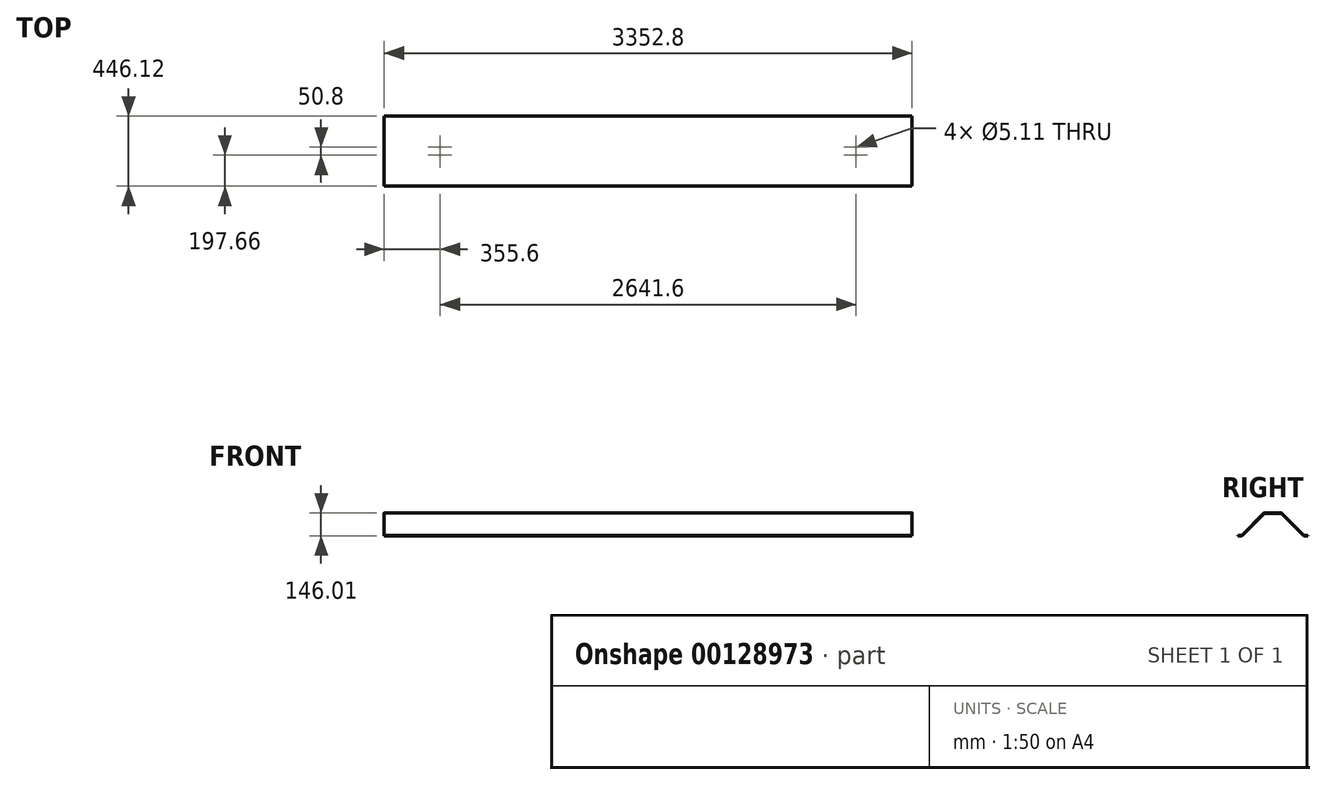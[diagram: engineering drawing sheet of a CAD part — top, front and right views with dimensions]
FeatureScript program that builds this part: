
annotation { "Feature Type Name" : "Feature", "Feature Type Description" : "" }
export const myFeature = defineFeature(function(context is Context, id is Id, definition is map)
    precondition{}
    {
        {
            var Q0;
            Q0=qCreatedBy(makeId("Right.planeOp"),FACE);
            var sketch = newSketch(context, id + "F0", { "sketchPlane" : qUnion([Q0])});
            skLineSegment(sketch, "E0", {"start": v(0, 146) * mm, "end": v(54.94, 146) * mm});
            skLineSegment(sketch, "E1", {"start": v(54.94, 146) * mm, "end": v(198.62, 2.32) * mm});
            skLineSegment(sketch, "E2", {"start": v(198.62, 2.32) * mm, "end": v(223.06, 2.32) * mm});
            skLineSegment(sketch, "E3", {"start": v(223.06, 2.32) * mm, "end": v(223.06, 0) * mm});
            skLineSegment(sketch, "E4", {"start": v(223.06, 0) * mm, "end": v(197.66, 0) * mm});
            skLineSegment(sketch, "E5", {"start": v(197.66, 0) * mm, "end": v(53.97, 143.68) * mm});
            skLineSegment(sketch, "E6", {"start": v(53.98, 143.68) * mm, "end": v(0, 143.68) * mm});
            skLineSegment(sketch, "E7", {"start": v(0, 143.68) * mm, "end": v(0, 146) * mm});
            skLineSegment(sketch, "E8", {"start": v(62.94, 134.72) * mm, "end": v(64.58, 136.37) * mm});
            skSolve(sketch);
        }
        {
            var Q0;
            {var subQ1=sQuery(id+"F0.wireOp",EDGE,"E2");Q0=makeQuery(id+"F0.imprint","IMPRINT",FACE,{"disambiguationData":[TD([[makeQuery(id+"F0.imprint","IMPRINT",EDGE,{"derivedFrom":subQ1}),-1.0]])]});}
            var Q1;
            {var subQ2=sQuery(id+"F0.wireOp",EDGE,"E0");Q1=makeQuery(id+"F0.imprint","IMPRINT",FACE,{"disambiguationData":[TD([[makeQuery(id+"F0.imprint","IMPRINT",EDGE,{"derivedFrom":subQ2}),-1.0]])]});}
            extrude(context, id + "F1", {"entities" : qUnion([Q0, Q1]), "endBound" : BoundingType.SYMMETRIC, "depth" : 3352.8 * mm});
        }
        {
            var Q0;
            Q0=makeQuery(id+"F1.opExtrude","SWEPT_BODY",BODY,{"disambiguationData":[OSD([sQuery(id+"F0.wireOp",EDGE,"E0"),sQuery(id+"F0.wireOp",EDGE,"E1"),sQuery(id+"F0.wireOp",EDGE,"E2"),sQuery(id+"F0.wireOp",EDGE,"E3"),sQuery(id+"F0.wireOp",EDGE,"E4"),sQuery(id+"F0.wireOp",EDGE,"E5"),sQuery(id+"F0.wireOp",EDGE,"E6"),sQuery(id+"F0.wireOp",EDGE,"E7")])]});
            var Q1;
            Q1=makeQuery(id+"F1.opExtrude","SWEPT_FACE",FACE,{"disambiguationData":[OSD([sQuery(id+"F0.wireOp",EDGE,"E7")])]});
            mirror(context, id + "F2", {"operationType" : NewBodyOperationType.ADD, "entities" : qUnion([Q0]), "mirrorPlane" : qUnion([Q1])});
        }
        {
            var Q0;
            Q0=makeQuery(id+"F2.opPattern","COPY",EDGE,{"derivedFrom":makeQuery(id+"F1.opExtrude","SWEPT_EDGE",EDGE,{"disambiguationData":[OSD([sQuery(id+"F0.wireOp",EDGE,"E0"),sQuery(id+"F0.wireOp",EDGE,"E1")])]}),"instanceName":"1"});
            var Q1;
            Q1=makeQuery(id+"F2.opPattern","COPY",EDGE,{"derivedFrom":makeQuery(id+"F1.opExtrude","SWEPT_EDGE",EDGE,{"disambiguationData":[OSD([sQuery(id+"F0.wireOp",EDGE,"E1"),sQuery(id+"F0.wireOp",EDGE,"E2")])]}),"instanceName":"1"});
            var Q2;
            Q2=makeQuery(id+"F1.opExtrude","SWEPT_EDGE",EDGE,{"disambiguationData":[OSD([sQuery(id+"F0.wireOp",EDGE,"E0"),sQuery(id+"F0.wireOp",EDGE,"E1")])]});
            var Q3;
            Q3=makeQuery(id+"F1.opExtrude","SWEPT_EDGE",EDGE,{"disambiguationData":[OSD([sQuery(id+"F0.wireOp",EDGE,"E1"),sQuery(id+"F0.wireOp",EDGE,"E2")])]});
            var Q4;
            Q4=makeQuery(id+"F2.opPattern","COPY",EDGE,{"derivedFrom":makeQuery(id+"F1.opExtrude","SWEPT_EDGE",EDGE,{"disambiguationData":[OSD([sQuery(id+"F0.wireOp",EDGE,"E4"),sQuery(id+"F0.wireOp",EDGE,"E5")])]}),"instanceName":"1"});
            var Q5;
            Q5=makeQuery(id+"F1.opExtrude","SWEPT_EDGE",EDGE,{"disambiguationData":[OSD([sQuery(id+"F0.wireOp",EDGE,"E4"),sQuery(id+"F0.wireOp",EDGE,"E5")])]});
            fillet(context, id + "F3", {"entities" : qUnion([Q0, Q1, Q2, Q3, Q4, Q5]), "radius" : 3.17 * mm, "tangentPropagation" : true, "allowEdgeOverflow" : false});
        }
        {
            var Q0;
            Q0=makeQuery(id+"F2.opPattern","COPY",EDGE,{"derivedFrom":makeQuery(id+"F1.opExtrude","SWEPT_EDGE",EDGE,{"disambiguationData":[OSD([sQuery(id+"F0.wireOp",EDGE,"E5"),sQuery(id+"F0.wireOp",EDGE,"E6")])]}),"instanceName":"1"});
            var Q1;
            Q1=makeQuery(id+"F1.opExtrude","SWEPT_EDGE",EDGE,{"disambiguationData":[OSD([sQuery(id+"F0.wireOp",EDGE,"E5"),sQuery(id+"F0.wireOp",EDGE,"E6")])]});
            fillet(context, id + "F4", {"entities" : qUnion([Q0, Q1]), "radius" : 3.17 * mm, "tangentPropagation" : true, "allowEdgeOverflow" : false});
        }
        {
            var Q0;
            {var subQ0=makeQuery(id+"F1.opExtrude","SWEPT_FACE",FACE,{"disambiguationData":[OSD([sQuery(id+"F0.wireOp",EDGE,"E0")])]});Q0=makeQuery(id+"F2.boolean.opBoolean","MERGE",FACE,{"derivedFrom":[subQ0,makeQuery(id+"F2.opPattern","COPY",FACE,{"derivedFrom":subQ0,"instanceName":"1"})]});}
            var sketch = newSketch(context, id + "F5", { "sketchPlane" : qUnion([Q0])});
            skPoint(sketch, "E9", {"position": v(-1320.8, 25.4) * mm});
            skPoint(sketch, "E10", {"position": v(-1320.8, -25.4) * mm});
            skPoint(sketch, "E11", {"position": v(1320.8, 25.4) * mm});
            skPoint(sketch, "E12", {"position": v(1320.8, -25.4) * mm});
            skLineSegment(sketch, "E13", {"start": v(107.92, 0) * mm, "end": v(-112.77, 0) * mm});
            skLineSegment(sketch, "E14", {"start": v(0, -22.88) * mm, "end": v(0, 26.34) * mm});
            skPoint(sketch, "E14.endSnap0", {"position": v(0, 53.62) * mm});
            skLineSegment(sketch, "E15", {"start": v(1320.8, -25.4) * mm, "end": v(1320.8, 25.4) * mm});
            skLineSegment(sketch, "E16", {"start": v(1320.8, 25.4) * mm, "end": v(-1320.8, 25.4) * mm});
            skSolve(sketch);
        }
        {
            var Q0;
            Q0=sQuery(id+"F5.wireOp",VERTEX,"E9");
            var Q1;
            Q1=sQuery(id+"F5.wireOp",VERTEX,"E10");
            var Q2;
            Q2=sQuery(id+"F5.wireOp",VERTEX,"E11");
            var Q3;
            Q3=sQuery(id+"F5.wireOp",VERTEX,"E12");
            var Q4;
            Q4=makeQuery(id+"F1.opExtrude","SWEPT_BODY",BODY,{"disambiguationData":[OSD([sQuery(id+"F0.wireOp",EDGE,"E0"),sQuery(id+"F0.wireOp",EDGE,"E1"),sQuery(id+"F0.wireOp",EDGE,"E2"),sQuery(id+"F0.wireOp",EDGE,"E3"),sQuery(id+"F0.wireOp",EDGE,"E4"),sQuery(id+"F0.wireOp",EDGE,"E5"),sQuery(id+"F0.wireOp",EDGE,"E6"),sQuery(id+"F0.wireOp",EDGE,"E7")])]});
            hole(context, id + "F6", {"style" : HoleStyle.SIMPLE, "endStyle" : HoleEndStyle.THROUGH, "standardTappedOrClearance" : lookupTablePath({ "standard" : "ANSI", "engagement" : "75%", "pitch" : "20 tpi", "size" : "1/4", "type" : "Tapped" }), "standardBlindInLast" : lookupTablePath({ "standard" : "ANSI", "engagement" : "75%", "pitch" : "20 tpi", "size" : "1/4", "type" : "Tapped" }), "holeDiameter" : 5.1 * mm, "locations" : qUnion([Q0, Q1, Q2, Q3]), "scope" : qUnion([Q4]), "isTappedThrough" : true, "majorDiameter" : 6.35 * mm, "showTappedDepth" : true});
        }
    });
